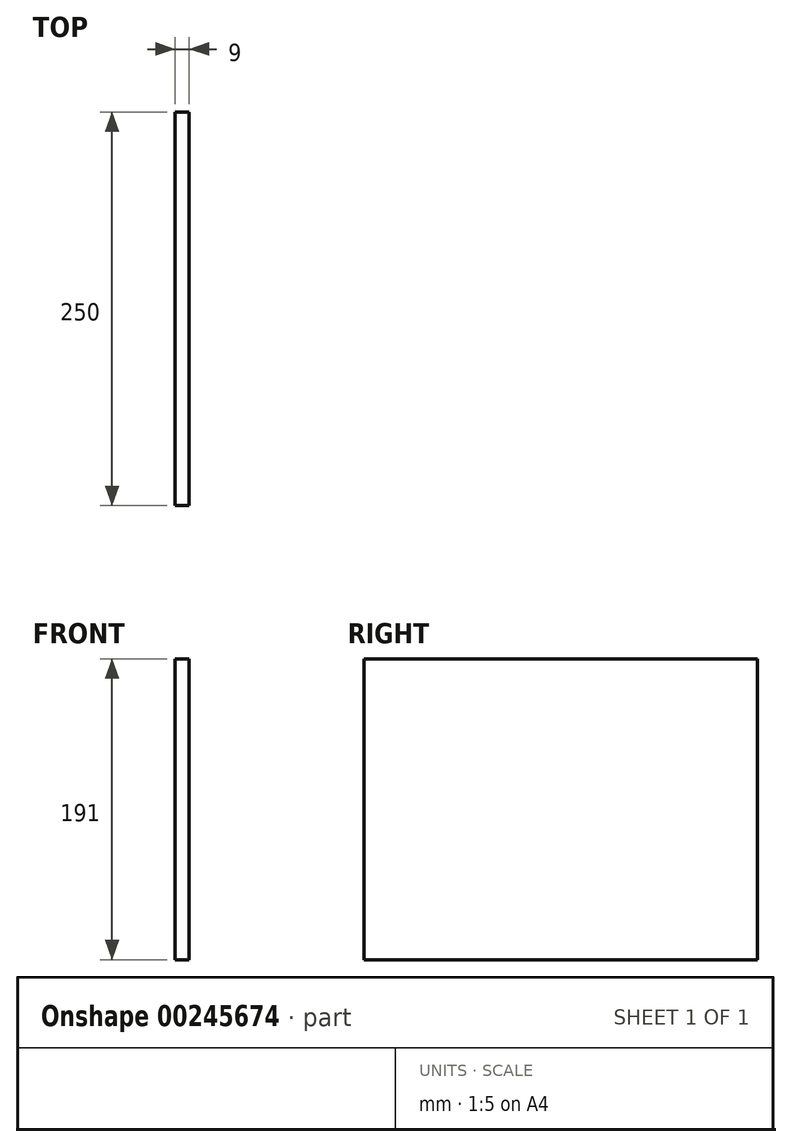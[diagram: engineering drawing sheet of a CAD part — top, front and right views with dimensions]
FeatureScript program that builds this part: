
annotation { "Feature Type Name" : "Feature", "Feature Type Description" : "" }
export const myFeature = defineFeature(function(context is Context, id is Id, definition is map)
    precondition{}
    {
        {
            var Q0;
            Q0=qCreatedBy(makeId("Right.planeOp"),FACE);
            var sketch = newSketch(context, id + "F0", { "sketchPlane" : qUnion([Q0])});
            skLineSegment(sketch, "E0.bottom", {"start": v(125, -95.5) * mm, "end": v(-125, -95.5) * mm});
            skLineSegment(sketch, "E0.top", {"start": v(125, 95.5) * mm, "end": v(-125, 95.5) * mm});
            skLineSegment(sketch, "E0.left", {"start": v(125, -95.5) * mm, "end": v(125, 95.5) * mm});
            skLineSegment(sketch, "E0.right", {"start": v(-125, -95.5) * mm, "end": v(-125, 95.5) * mm});
            skPoint(sketch, "E0.middle", {"position": v(0, 0) * mm});
            skSolve(sketch);
        }
        {
            var Q0;
            Q0 = qSketchRegion(id + "F0", true);
            extrude(context, id + "F1", {"entities" : qUnion([Q0]), "depth" : 9 * mm});
        }
    });
